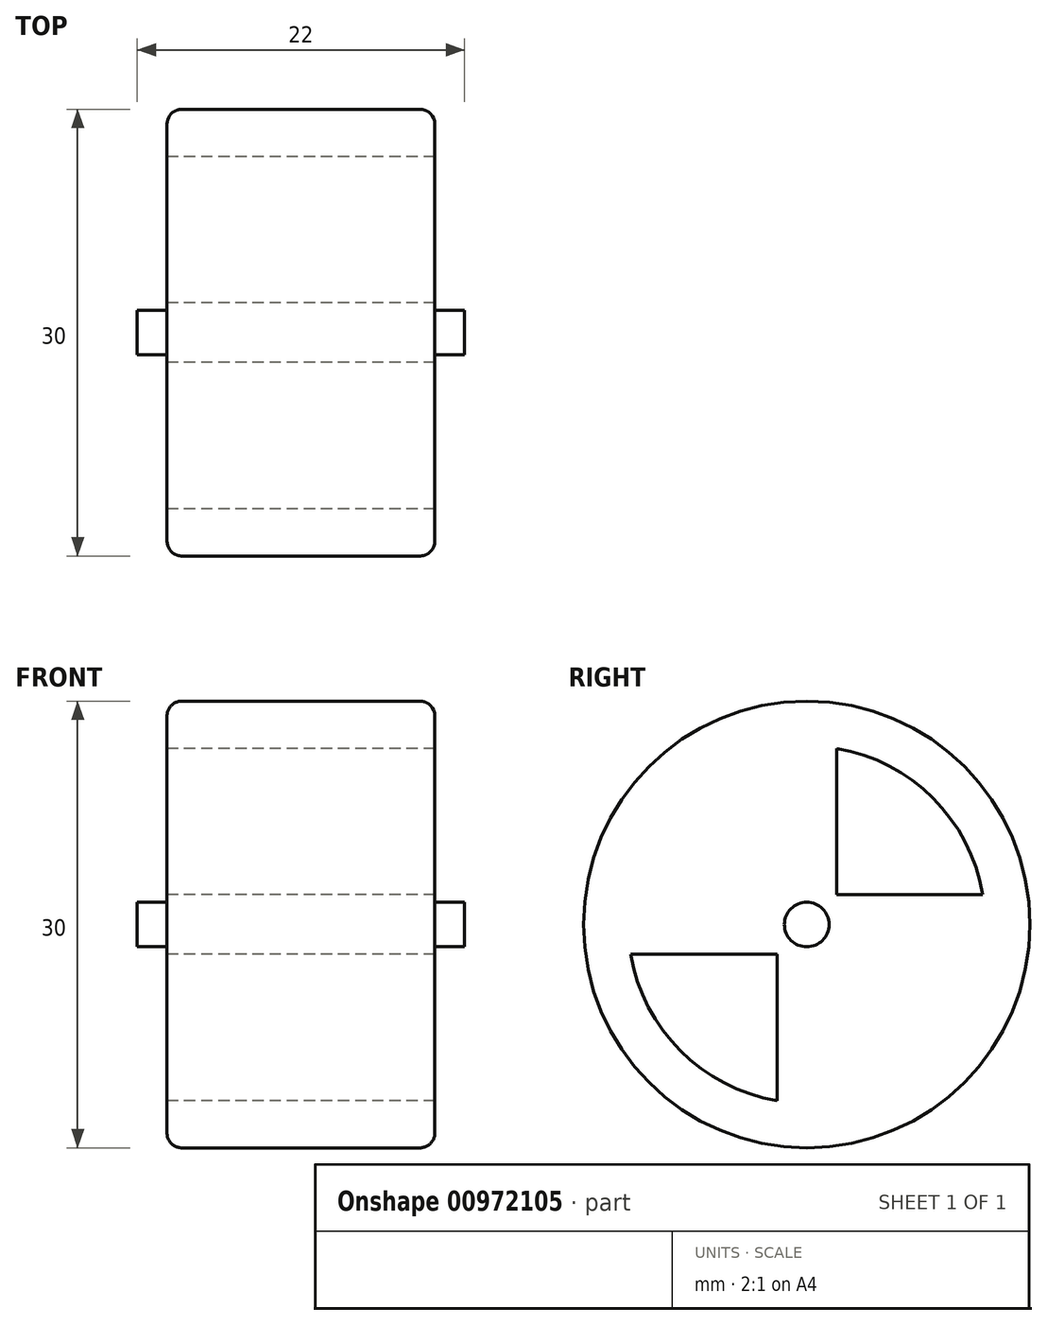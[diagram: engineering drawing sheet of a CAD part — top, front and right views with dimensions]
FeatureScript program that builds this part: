
annotation { "Feature Type Name" : "Feature", "Feature Type Description" : "" }
export const myFeature = defineFeature(function(context is Context, id is Id, definition is map)
    precondition{}
    {
        {
            var Q0;
            Q0=qCreatedBy(makeId("Right.planeOp"),FACE);
            var sketch = newSketch(context, id + "F0", { "sketchPlane" : qUnion([Q0])});
            skCircle(sketch, "E0", {"center": v(0, 0) * mm, "radius": 15 * mm});
            skCircle(sketch, "E1", {"center": v(0, 0) * mm, "radius": 1.5 * mm});
            skLineSegment(sketch, "E2", {"start": v(0, 15) * mm, "end": v(0, -15) * mm, "construction": true});
            skLineSegment(sketch, "E3", {"start": v(15, 0) * mm, "end": v(-15, 0) * mm, "construction": true});
            skLineSegment(sketch, "E4.0", {"start": v(15, 2) * mm, "end": v(14.87, 2) * mm});
            skLineSegment(sketch, "E5.0", {"start": v(2, 15) * mm, "end": v(2, 14.87) * mm});
            skArc(sketch, "E6.0", {"start": v(-11.83, -2) * mm, "mid": v(-8.49, -8.49) * mm, "end": v(-2, -11.83) * mm});
            skLineSegment(sketch, "E7.0", {"start": v(-2, 15) * mm, "end": v(-2, 14.87) * mm});
            skLineSegment(sketch, "E8.0", {"start": v(15, -2) * mm, "end": v(14.87, -2) * mm});
            skLineSegment(sketch, "E9.trimOffspring", {"start": v(-2, -2) * mm, "end": v(-11.83, -2) * mm});
            skLineSegment(sketch, "E10.trimOffspring", {"start": v(-2, -2) * mm, "end": v(-2, -11.83) * mm});
            skLineSegment(sketch, "E11.trimOffspring", {"start": v(-14.87, -2) * mm, "end": v(-15, -2) * mm});
            skLineSegment(sketch, "E12.trimOffspring", {"start": v(-2, -14.87) * mm, "end": v(-2, -15) * mm});
            skLineSegment(sketch, "E13.trimOffspring", {"start": v(2, -14.87) * mm, "end": v(2, -15) * mm});
            skLineSegment(sketch, "E14.trimOffspring", {"start": v(11.83, 2) * mm, "end": v(2, 2) * mm});
            skLineSegment(sketch, "E15.trimOffspring", {"start": v(-14.87, 2) * mm, "end": v(-15, 2) * mm});
            skArc(sketch, "E16.trimOffspring", {"start": v(11.83, 2) * mm, "mid": v(8.49, 8.49) * mm, "end": v(2, 11.83) * mm});
            skLineSegment(sketch, "E17.trimOffspring", {"start": v(2, 11.83) * mm, "end": v(2, 2) * mm});
            skSolve(sketch);
        }
        {
            var Q0;
            Q0=makeQuery(id+"F0.imprint","IMPRINT",FACE,{"disambiguationData":[TD([[makeQuery(id+"F0.imprint","IMPRINT",EDGE,{"derivedFrom":sQuery(id+"F0.wireOp",EDGE,"E0")}),1.0]])]});
            extrude(context, id + "F1", {"entities" : qUnion([Q0]), "depth" : 18 * mm, "offsetDistance" : 25 * mm});
        }
        {
            var Q0;
            Q0=makeQuery(id+"F1.opExtrude","CAP_EDGE",EDGE,{"disambiguationData":[OSD([sQuery(id+"F0.wireOp",EDGE,"E0")])],"isStart":true});
            var Q1;
            Q1=makeQuery(id+"F1.opExtrude","CAP_EDGE",EDGE,{"disambiguationData":[OSD([sQuery(id+"F0.wireOp",EDGE,"E0")])],"isStart":false});
            fillet(context, id + "F2", {"entities" : qUnion([Q0, Q1]), "radius" : 1 * mm, "tangentPropagation" : true, "allowEdgeOverflow" : false});
        }
        {
            var Q0;
            Q0=makeQuery(id+"F0.imprint","IMPRINT",FACE,{"disambiguationData":[TD([[makeQuery(id+"F0.imprint","IMPRINT",EDGE,{"derivedFrom":sQuery(id+"F0.wireOp",EDGE,"E1")}),1.0]])]});
            extrude(context, id + "F3", {"entities" : qUnion([Q0]), "operationType" : NewBodyOperationType.ADD, "depth" : 20 * mm, "offsetDistance" : 25 * mm});
        }
        {
            var Q0;
            Q0=makeQuery(id+"F0.imprint","IMPRINT",FACE,{"disambiguationData":[TD([[makeQuery(id+"F0.imprint","IMPRINT",EDGE,{"derivedFrom":sQuery(id+"F0.wireOp",EDGE,"E1")}),1.0]])]});
            extrude(context, id + "F4", {"entities" : qUnion([Q0]), "operationType" : NewBodyOperationType.ADD, "oppositeDirection" : true, "depth" : 2 * mm, "offsetDistance" : 25 * mm});
        }
    });
